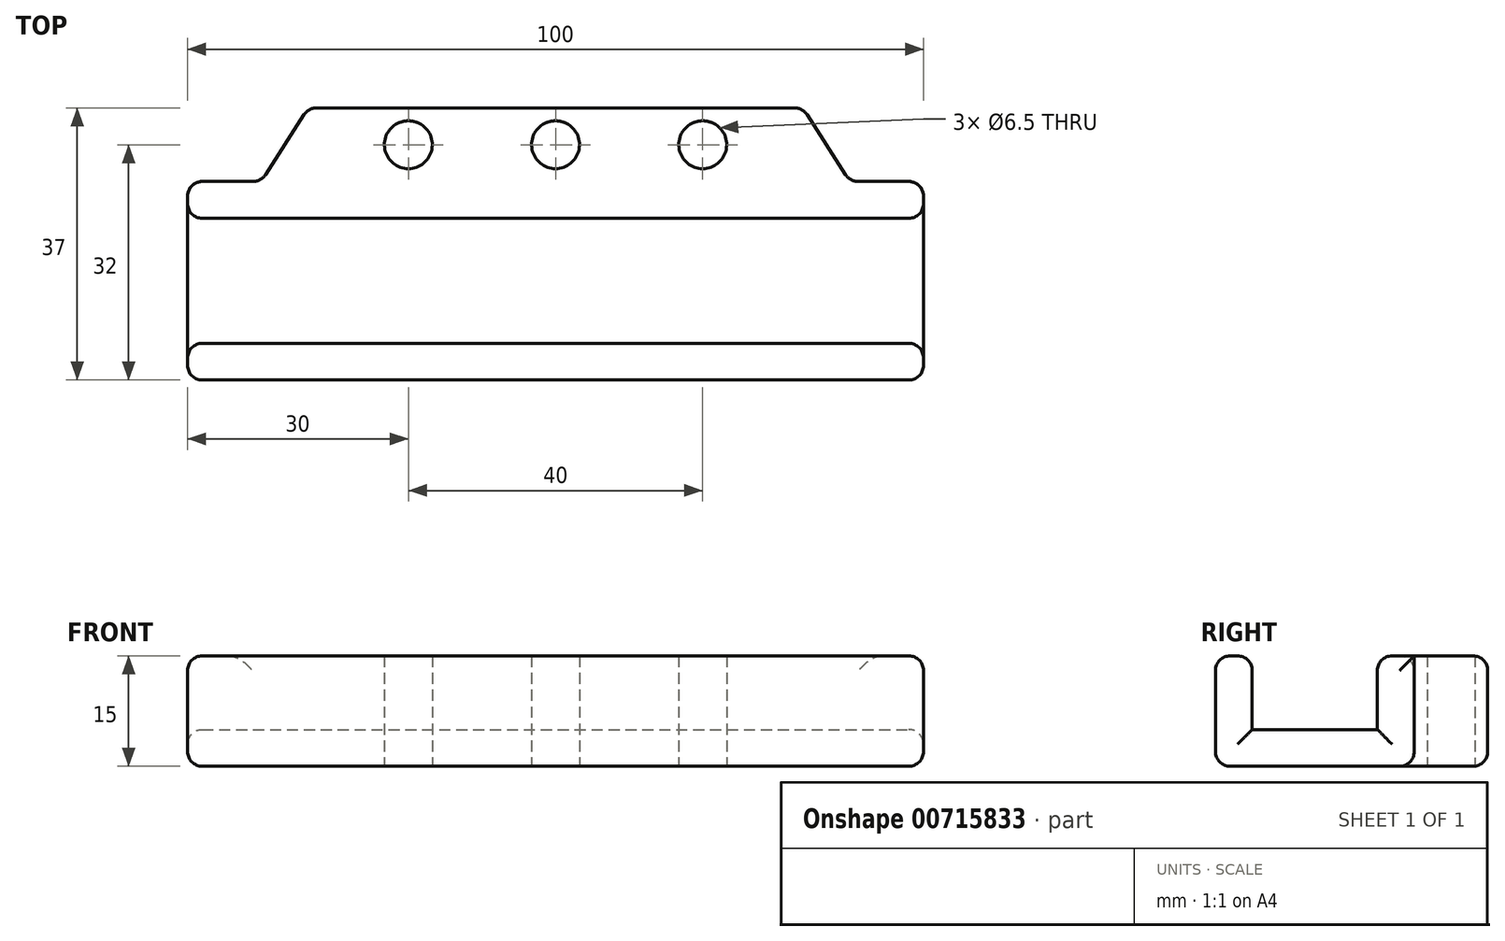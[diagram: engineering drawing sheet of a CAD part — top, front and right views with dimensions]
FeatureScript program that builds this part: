
annotation { "Feature Type Name" : "Feature", "Feature Type Description" : "" }
export const myFeature = defineFeature(function(context is Context, id is Id, definition is map)
    precondition{}
    {
        {
            var Q0;
            Q0=qCreatedBy(makeId("Top.planeOp"),FACE);
            var sketch = newSketch(context, id + "F0", { "sketchPlane" : qUnion([Q0])});
            skLineSegment(sketch, "E0.bottom", {"start": v(-50, 13.5) * mm, "end": v(50, 13.5) * mm});
            skLineSegment(sketch, "E0.top", {"start": v(-50, -13.5) * mm, "end": v(50, -13.5) * mm});
            skLineSegment(sketch, "E0.left", {"start": v(-50, 13.5) * mm, "end": v(-50, -13.5) * mm});
            skLineSegment(sketch, "E0.right", {"start": v(50, 13.5) * mm, "end": v(50, -13.5) * mm});
            skPoint(sketch, "E0.middle", {"position": v(0, 0) * mm});
            skPoint(sketch, "E1", {"position": v(0, 13.5) * mm});
            skPoint(sketch, "E2", {"position": v(-40, 13.5) * mm});
            skPoint(sketch, "E3", {"position": v(40, 13.5) * mm});
            skPoint(sketch, "E4", {"position": v(-20, 13.5) * mm});
            skPoint(sketch, "E5", {"position": v(20, 13.5) * mm});
            skPoint(sketch, "E6", {"position": v(50, -8.5) * mm});
            skPoint(sketch, "E7", {"position": v(-50, -8.5) * mm});
            skPoint(sketch, "E8", {"position": v(50, 8.5) * mm});
            skPoint(sketch, "E9", {"position": v(-50, 8.5) * mm});
            skLineSegment(sketch, "E10", {"start": v(-50, 8.5) * mm, "end": v(50, 8.5) * mm});
            skLineSegment(sketch, "E11", {"start": v(50, -8.5) * mm, "end": v(-50, -8.5) * mm});
            skPoint(sketch, "E12", {"position": v(20, 23.5) * mm});
            skPoint(sketch, "E13", {"position": v(0, 23.5) * mm});
            skPoint(sketch, "E14", {"position": v(-20, 23.5) * mm});
            skPoint(sketch, "E15", {"position": v(-33.6, 23.5) * mm});
            skPoint(sketch, "E16", {"position": v(33.6, 23.5) * mm});
            skLineSegment(sketch, "E17", {"start": v(-33.6, 23.5) * mm, "end": v(33.6, 23.5) * mm});
            skPoint(sketch, "E18", {"position": v(-20, 18.5) * mm});
            skPoint(sketch, "E19", {"position": v(0, 18.5) * mm});
            skPoint(sketch, "E20", {"position": v(20, 18.5) * mm});
            skCircle(sketch, "E21", {"center": v(-20, 18.5) * mm, "radius": 3.25 * mm});
            skCircle(sketch, "E22", {"center": v(0, 18.5) * mm, "radius": 3.25 * mm});
            skCircle(sketch, "E23", {"center": v(20, 18.5) * mm, "radius": 3.25 * mm});
            skLineSegment(sketch, "E24", {"start": v(-33.6, 23.5) * mm, "end": v(-40, 13.5) * mm});
            skLineSegment(sketch, "E25", {"start": v(33.6, 23.5) * mm, "end": v(40, 13.5) * mm});
            skSolve(sketch);
        }
        {
            var Q0;
            Q0=makeQuery(id+"F0.imprint","IMPRINT",FACE,{"disambiguationData":[TD([[makeQuery(id+"F0.imprint","IMPRINT",EDGE,{"derivedFrom":sQuery(id+"F0.wireOp",EDGE,"E17")}),-1.0]])]});
            var Q1;
            {var subQ3=sQuery(id+"F0.wireOp",EDGE,"E10");Q1=makeQuery(id+"F0.imprint","IMPRINT",FACE,{"disambiguationData":[TD([[makeQuery(id+"F0.imprint","IMPRINT",EDGE,{"derivedFrom":subQ3}),1.0]])]});}
            var Q2;
            {var subQ0=sQuery(id+"F0.wireOp",EDGE,"E10");Q2=makeQuery(id+"F0.imprint","IMPRINT",FACE,{"disambiguationData":[TD([[makeQuery(id+"F0.imprint","IMPRINT",EDGE,{"derivedFrom":subQ0}),-1.0]])]});}
            var Q3;
            {var subQ0=sQuery(id+"F0.wireOp",EDGE,"E0.top");Q3=makeQuery(id+"F0.imprint","IMPRINT",FACE,{"disambiguationData":[TD([[makeQuery(id+"F0.imprint","IMPRINT",EDGE,{"derivedFrom":subQ0}),1.0]])]});}
            extrude(context, id + "F1", {"entities" : qUnion([Q0, Q1, Q2, Q3]), "depth" : 5 * mm, "offsetDistance" : 25 * mm});
        }
        {
            var Q0;
            Q0=makeQuery(id+"F0.imprint","IMPRINT",FACE,{"disambiguationData":[TD([[makeQuery(id+"F0.imprint","IMPRINT",EDGE,{"derivedFrom":sQuery(id+"F0.wireOp",EDGE,"E17")}),-1.0]])]});
            var Q1;
            {var subQ3=sQuery(id+"F0.wireOp",EDGE,"E10");Q1=makeQuery(id+"F0.imprint","IMPRINT",FACE,{"disambiguationData":[TD([[makeQuery(id+"F0.imprint","IMPRINT",EDGE,{"derivedFrom":subQ3}),1.0]])]});}
            var Q2;
            {var subQ0=sQuery(id+"F0.wireOp",EDGE,"E0.top");Q2=makeQuery(id+"F0.imprint","IMPRINT",FACE,{"disambiguationData":[TD([[makeQuery(id+"F0.imprint","IMPRINT",EDGE,{"derivedFrom":subQ0}),1.0]])]});}
            extrude(context, id + "F2", {"entities" : qUnion([Q0, Q1, Q2]), "operationType" : NewBodyOperationType.ADD, "depth" : 15 * mm, "offsetDistance" : 25 * mm});
        }
        {
            var Q0;
            Q0=makeQuery(id+"F1.opExtrude","CAP_EDGE",EDGE,{"disambiguationData":[OSD([sQuery(id+"F0.wireOp",EDGE,"E0.right")])],"isStart":true});
            var Q1;
            {var subQ0=sQuery(id+"F0.wireOp",EDGE,"E0.bottom");Q1=makeQuery(id+"F1.opExtrude","CAP_EDGE",EDGE,{"disambiguationData":[OSD([subQ0]),TDD([makeQuery(id+"F0.imprint","IMPRINT",EDGE,{"disambiguationData":[TD([[makeQuery(id+"F0.imprint","INTERSECT",VERTEX,{"derivedFrom":[subQ0,sQuery(id+"F0.wireOp",EDGE,"E0.right")]}),1.0]])],"derivedFrom":subQ0})])],"isStart":true});}
            var Q2;
            Q2=makeQuery(id+"F1.opExtrude","CAP_EDGE",EDGE,{"disambiguationData":[OSD([sQuery(id+"F0.wireOp",EDGE,"E25")])],"isStart":true});
            var Q3;
            Q3=makeQuery(id+"F1.opExtrude","CAP_EDGE",EDGE,{"disambiguationData":[OSD([sQuery(id+"F0.wireOp",EDGE,"E17")])],"isStart":true});
            var Q4;
            Q4=makeQuery(id+"F1.opExtrude","CAP_EDGE",EDGE,{"disambiguationData":[OSD([sQuery(id+"F0.wireOp",EDGE,"E24")])],"isStart":true});
            var Q5;
            {var subQ0=sQuery(id+"F0.wireOp",EDGE,"E0.bottom");Q5=makeQuery(id+"F1.opExtrude","CAP_EDGE",EDGE,{"disambiguationData":[OSD([subQ0]),TDD([makeQuery(id+"F0.imprint","IMPRINT",EDGE,{"disambiguationData":[TD([[makeQuery(id+"F0.imprint","INTERSECT",VERTEX,{"derivedFrom":[subQ0,sQuery(id+"F0.wireOp",EDGE,"E0.left")]}),-1.0]])],"derivedFrom":subQ0})])],"isStart":true});}
            var Q6;
            Q6=makeQuery(id+"F1.opExtrude","CAP_EDGE",EDGE,{"disambiguationData":[OSD([sQuery(id+"F0.wireOp",EDGE,"E0.left")])],"isStart":true});
            var Q7;
            Q7=makeQuery(id+"F1.opExtrude","CAP_EDGE",EDGE,{"disambiguationData":[OSD([sQuery(id+"F0.wireOp",EDGE,"E0.top")])],"isStart":true});
            var Q8;
            {var subQ0=sQuery(id+"F0.wireOp",EDGE,"E24");Q8=makeQuery(id+"F2.boolean.opBoolean","MERGE",FACE,{"derivedFrom":[makeQuery(id+"F1.opExtrude","SWEPT_FACE",FACE,{"disambiguationData":[OSD([subQ0])]}),makeQuery(id+"F2.opExtrude","SWEPT_FACE",FACE,{"disambiguationData":[OSD([subQ0])]})]});}
            var Q9;
            {var subQ0=sQuery(id+"F0.wireOp",EDGE,"E0.left");Q9=makeQuery(id+"F2.boolean.opBoolean","MERGE",FACE,{"derivedFrom":[makeQuery(id+"F1.opExtrude","SWEPT_FACE",FACE,{"disambiguationData":[OSD([subQ0])]}),makeQuery(id+"F2.opExtrude","SWEPT_FACE",FACE,{"disambiguationData":[OSD([subQ0]),TDD([makeQuery(id+"F0.imprint","IMPRINT",EDGE,{"disambiguationData":[TD([[makeQuery(id+"F0.imprint","INTERSECT",VERTEX,{"derivedFrom":[sQuery(id+"F0.wireOp",EDGE,"E0.bottom"),subQ0]}),-1.0]])],"derivedFrom":subQ0})])]}),makeQuery(id+"F2.opExtrude","SWEPT_FACE",FACE,{"disambiguationData":[OSD([subQ0]),TDD([makeQuery(id+"F0.imprint","IMPRINT",EDGE,{"disambiguationData":[TD([[makeQuery(id+"F0.imprint","INTERSECT",VERTEX,{"derivedFrom":[sQuery(id+"F0.wireOp",EDGE,"E0.top"),subQ0]}),1.0]])],"derivedFrom":subQ0})])]})]});}
            var Q10;
            {var subQ0=sQuery(id+"F0.wireOp",EDGE,"E25");Q10=makeQuery(id+"F2.boolean.opBoolean","MERGE",FACE,{"derivedFrom":[makeQuery(id+"F1.opExtrude","SWEPT_FACE",FACE,{"disambiguationData":[OSD([subQ0])]}),makeQuery(id+"F2.opExtrude","SWEPT_FACE",FACE,{"disambiguationData":[OSD([subQ0])]})]});}
            var Q11;
            {var subQ0=sQuery(id+"F0.wireOp",EDGE,"E0.right");Q11=makeQuery(id+"F2.boolean.opBoolean","MERGE",FACE,{"derivedFrom":[makeQuery(id+"F1.opExtrude","SWEPT_FACE",FACE,{"disambiguationData":[OSD([subQ0])]}),makeQuery(id+"F2.opExtrude","SWEPT_FACE",FACE,{"disambiguationData":[OSD([subQ0]),TDD([makeQuery(id+"F0.imprint","IMPRINT",EDGE,{"disambiguationData":[TD([[makeQuery(id+"F0.imprint","INTERSECT",VERTEX,{"derivedFrom":[sQuery(id+"F0.wireOp",EDGE,"E0.bottom"),subQ0]}),-1.0]])],"derivedFrom":subQ0})])]}),makeQuery(id+"F2.opExtrude","SWEPT_FACE",FACE,{"disambiguationData":[OSD([subQ0]),TDD([makeQuery(id+"F0.imprint","IMPRINT",EDGE,{"disambiguationData":[TD([[makeQuery(id+"F0.imprint","INTERSECT",VERTEX,{"derivedFrom":[sQuery(id+"F0.wireOp",EDGE,"E0.top"),subQ0]}),1.0]])],"derivedFrom":subQ0})])]})]});}
            var Q12;
            Q12=makeQuery(id+"F2.opExtrude","CAP_EDGE",EDGE,{"disambiguationData":[OSD([sQuery(id+"F0.wireOp",EDGE,"E10")])],"isStart":false});
            var Q13;
            Q13=makeQuery(id+"F2.opExtrude","CAP_FACE",FACE,{"disambiguationData":[OSD([sQuery(id+"F0.wireOp",EDGE,"E0.top"),sQuery(id+"F0.wireOp",EDGE,"E0.left"),sQuery(id+"F0.wireOp",EDGE,"E0.right"),sQuery(id+"F0.wireOp",EDGE,"E11")])],"isStart":false});
            var Q14;
            Q14=makeQuery(id+"F2.opExtrude","CAP_EDGE",EDGE,{"disambiguationData":[OSD([sQuery(id+"F0.wireOp",EDGE,"E17")])],"isStart":false});
            fillet(context, id + "F3", {"entities" : qUnion([Q0, Q1, Q2, Q3, Q4, Q5, Q6, Q7, Q8, Q9, Q10, Q11, Q12, Q13, Q14]), "radius" : 2 * mm, "tangentPropagation" : true, "allowEdgeOverflow" : false});
        }
    });
